# Revit family: 712-3550-001-DN40-100-DN60-150
name_source: partatom
category: Pipe Accessories
units: mm (PartAtom-declared; Revit-internal decimal feet)

## family parameters
Always vertical = Yes
Cut with Voids When Loaded = No
Part Type = Valve - Breaks Into
Round Connector Dimension = Use Diameter
Shared = No
Work Plane-Based = No

## types (4) — shared parameters
Body_wallthickness = 10 mm  [stored 0.0328084 ft]
DN04-100_PN10/16 = 712-0104-35-501060
DN150-80_PN10/16 = 712-0153-35-501060
DN60-150_PN10/16 = 712-0157-35-501060
DN65-150_PN10/16 = 712-0154-35-501060
Description_ = AVK REDUCER FLANGE
RF_Thick = 3 mm  [stored 0.00984252 ft]
Search_Table = 712-3550-001-DN40-100-DN60-150
URL product pages = https://www.avkvalves.com

## per-type parameters (varying)
| type | 040-100_PN10/16 | 060-150_PN10/16 | 065-150_PN10/16 | 150-080_PN10/16 | D | D1 | D2 | D3 | DN1 | DN1_ref | DN2 | DN2_ref | Dh | Dh2 | ID(Radius) | L | L1 | L2 | Nominal Diameter (DN) | Rf_Dia | Rf_Dia_2 | Rib |
| 712-0104-35-501060_DN040-100_PN10/16 | Yes | No | No | No | 110 mm | 73.333 mm | 44 mm  [stored 0.144357 ft] | 31.429 mm | 40 mm  [stored 0.131234 ft] | 20 mm  [stored 0.0656168 ft] | 100 mm | 50 mm  [stored 0.164042 ft] | 180 mm | 110 mm | 20.05 mm  [stored 0.0657808 ft] | 78 mm  [stored 0.255906 ft] | 30 mm  [stored 0.0984252 ft] | 15 mm  [stored 0.0492126 ft] | 40.1 mm  [stored 0.131562 ft] | 84 mm  [stored 0.275591 ft] | 56 mm  [stored 0.183727 ft] | 10.025 mm  [stored 0.0328904 ft] |
| 712-0153-35-501060_DN150-080_PN10/16 | No | No | No | Yes | 142.5 mm | 95 mm  [stored 0.31168 ft] | 57 mm  [stored 0.187008 ft] | 40.714 mm | 80 mm  [stored 0.262467 ft] | 40 mm  [stored 0.131234 ft] | 150 mm | 75 mm | 240 mm | 160 mm | 75.04 mm  [stored 0.246194 ft] | 78 mm  [stored 0.255906 ft] | 30 mm  [stored 0.0984252 ft] | 15 mm  [stored 0.0492126 ft] | 150.08 mm | 99 mm  [stored 0.324803 ft] | 66 mm  [stored 0.216535 ft] | 37.52 mm  [stored 0.123097 ft] |
| 712-0154-35-501060_DN065-150_PN10/16 | No | No | Yes | No | 142.5 mm | 95 mm  [stored 0.31168 ft] | 57 mm  [stored 0.187008 ft] | 40.714 mm | 65 mm  [stored 0.213255 ft] | 32.5 mm  [stored 0.106627 ft] | 150 mm | 75 mm | 240 mm | 145 mm | 32.575 mm | 86 mm  [stored 0.282152 ft] | 35 mm  [stored 0.114829 ft] | 17.5 mm  [stored 0.0574147 ft] | 65.15 mm  [stored 0.213747 ft] | 108 mm | 72 mm  [stored 0.23622 ft] | 16.288 mm |
| 712-0157-35-501060_DN060-150_PN10/16 | No | Yes | No | No | 142.5 mm | 95 mm  [stored 0.31168 ft] | 57 mm  [stored 0.187008 ft] | 40.714 mm | 60 mm  [stored 0.19685 ft] | 30 mm  [stored 0.0984252 ft] | 150 mm | 75 mm | 240 mm | 135 mm | 30.075 mm  [stored 0.0986713 ft] | 84 mm  [stored 0.275591 ft] | 33 mm  [stored 0.108268 ft] | 16.5 mm  [stored 0.0541339 ft] | 60.15 mm  [stored 0.197343 ft] | 108 mm | 72 mm  [stored 0.23622 ft] | 15.038 mm |

note: [stored X ft] marks values corroborated as IEEE doubles in the binary element streams (Revit-internal decimal feet)

## geometry (parser evidence)
native form markers: Sweep x31
no freeform markers — native parametric forms only
